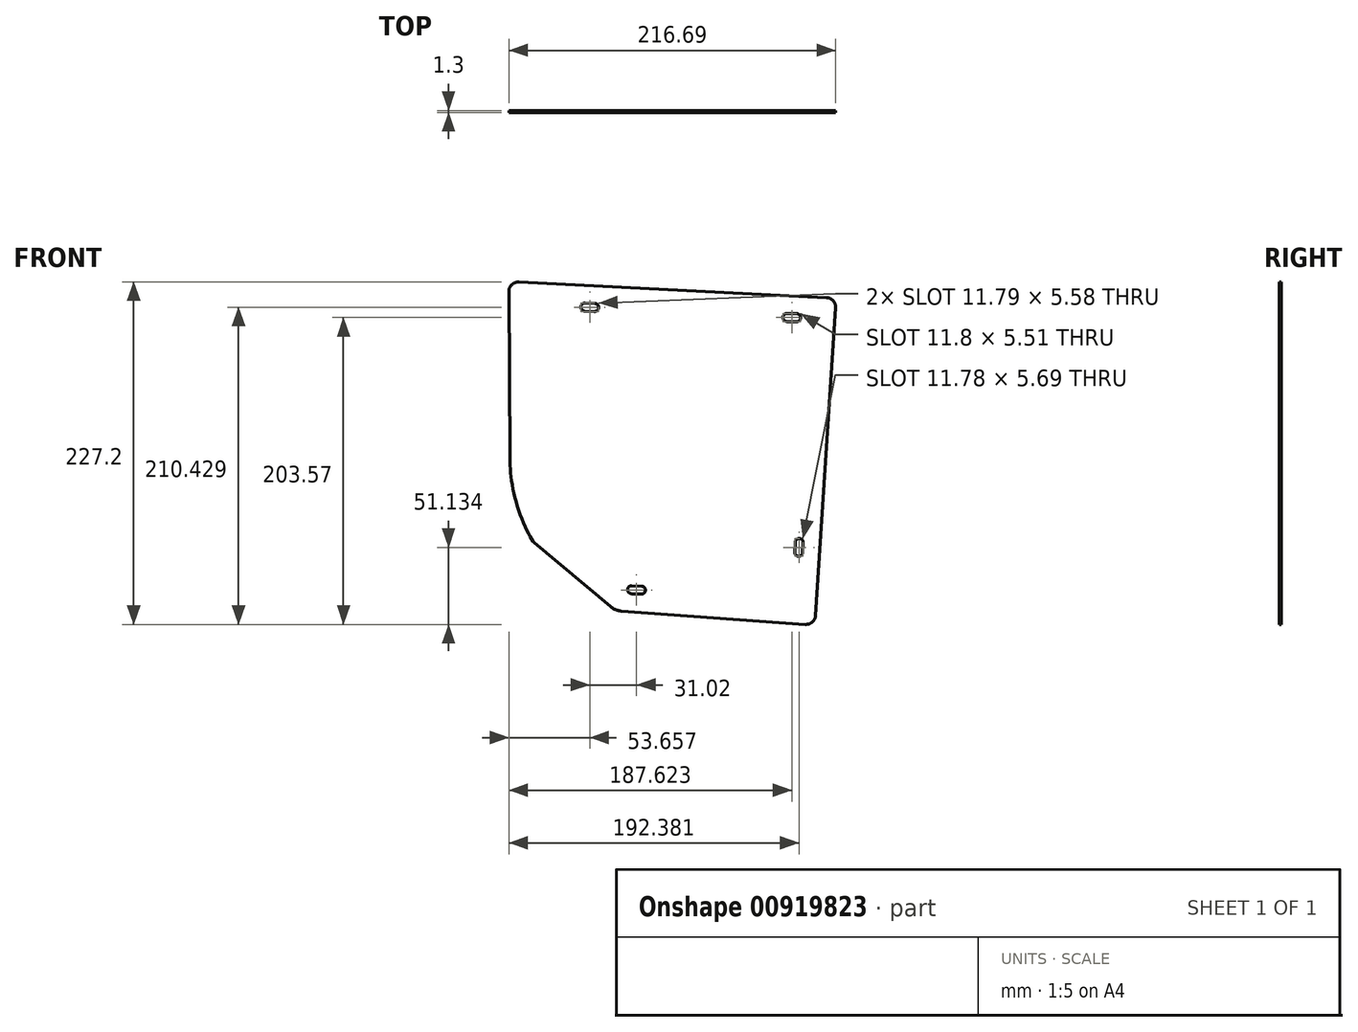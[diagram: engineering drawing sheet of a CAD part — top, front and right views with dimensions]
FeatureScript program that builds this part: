
annotation { "Feature Type Name" : "Feature", "Feature Type Description" : "" }
export const myFeature = defineFeature(function(context is Context, id is Id, definition is map)
    precondition{}
    {
        {
            var Q0;
            Q0=qCreatedBy(makeId("Front.planeOp"),FACE);
            var sketch = newSketch(context, id + "F0", { "sketchPlane" : qUnion([Q0])});
            skLineSegment(sketch, "E0", {"start": v(110.1, -168.08) * mm, "end": v(123.31, 36.08) * mm});
            skLineSegment(sketch, "E1", {"start": v(103.3, -174) * mm, "end": v(-18.7, -165.21) * mm});
            skLineSegment(sketch, "E2", {"start": v(-25.98, -162.25) * mm, "end": v(-76.3, -119.72) * mm});
            skPoint(sketch, "E3", {"position": v(-19.24, -165.17) * mm});
            skArc(sketch, "E4", {"start": v(-86.69, 53.17) * mm, "mid": v(-91.4, 51.42) * mm, "end": v(-93.36, 46.8) * mm});
            skArc(sketch, "E5", {"start": v(103.3, -174) * mm, "mid": v(107.94, -172.45) * mm, "end": v(110.1, -168.08) * mm});
            skArc(sketch, "E6.filletArc", {"start": v(-25.98, -162.25) * mm, "mid": v(-22.57, -164.3) * mm, "end": v(-18.7, -165.21) * mm});
            skArc(sketch, "E7", {"start": v(123.31, 36.08) * mm, "mid": v(121.72, 40.71) * mm, "end": v(117.3, 42.83) * mm});
            skLineSegment(sketch, "E8.trimOffspring", {"start": v(-86.69, 53.17) * mm, "end": v(117.3, 42.83) * mm});
            skFitSpline(sketch, "E9", {"points": [v(-92.68, -63.43) * mm, v(-87.67, -95.63) * mm, v(-76.3, -119.72) * mm], "startDerivative": vector(0.34, -55.65) * mm, "endDerivative": vector(20.09, -16.98) * mm});
            skArc(sketch, "E10", {"start": v(-42.83, 39.2) * mm, "mid": v(-45.6, 36.63) * mm, "end": v(-43.04, 33.87) * mm});
            skArc(sketch, "E11", {"start": v(-36.57, 33.62) * mm, "mid": v(-33.8, 36.18) * mm, "end": v(-36.37, 38.95) * mm});
            skLineSegment(sketch, "E12", {"start": v(-43.04, 33.87) * mm, "end": v(-36.57, 33.62) * mm});
            skLineSegment(sketch, "E13", {"start": v(-42.83, 39.2) * mm, "end": v(-36.37, 38.95) * mm});
            skArc(sketch, "E14", {"start": v(91.1, 32.3) * mm, "mid": v(88.36, 29.71) * mm, "end": v(90.96, 26.97) * mm});
            skArc(sketch, "E15", {"start": v(97.42, 26.8) * mm, "mid": v(100.16, 29.39) * mm, "end": v(97.57, 32.13) * mm});
            skLineSegment(sketch, "E16", {"start": v(90.96, 26.97) * mm, "end": v(97.42, 26.8) * mm});
            skLineSegment(sketch, "E17", {"start": v(91.1, 32.3) * mm, "end": v(97.57, 32.13) * mm});
            skArc(sketch, "E18", {"start": v(-11.81, -148.36) * mm, "mid": v(-14.58, -150.92) * mm, "end": v(-12.02, -153.69) * mm});
            skArc(sketch, "E19", {"start": v(-5.55, -153.94) * mm, "mid": v(-2.79, -151.37) * mm, "end": v(-5.35, -148.6) * mm});
            skLineSegment(sketch, "E20", {"start": v(-12.02, -153.69) * mm, "end": v(-5.55, -153.94) * mm});
            skLineSegment(sketch, "E21", {"start": v(-11.81, -148.36) * mm, "end": v(-5.35, -148.6) * mm});
            skArc(sketch, "E22", {"start": v(96.18, -125.97) * mm, "mid": v(98.7, -128.78) * mm, "end": v(101.5, -126.26) * mm});
            skArc(sketch, "E23", {"start": v(101.86, -119.8) * mm, "mid": v(99.35, -117) * mm, "end": v(96.54, -119.5) * mm});
            skLineSegment(sketch, "E24", {"start": v(101.5, -126.26) * mm, "end": v(101.86, -119.8) * mm});
            skLineSegment(sketch, "E25", {"start": v(96.18, -125.97) * mm, "end": v(96.54, -119.5) * mm});
            skLineSegment(sketch, "E26.trimOffspring", {"start": v(-92.68, -63.43) * mm, "end": v(-93.36, 46.8) * mm});
            skSolve(sketch);
        }
        {
            var Q0;
            Q0=makeQuery(id+"F0.imprint","IMPRINT",FACE,{"disambiguationData":[TD([[makeQuery(id+"F0.imprint","IMPRINT",EDGE,{"derivedFrom":sQuery(id+"F0.wireOp",EDGE,"E0")}),1.0]])]});
            extrude(context, id + "F1", {"entities" : qUnion([Q0]), "depth" : 1.3 * mm, "offsetDistance" : 25.4 * mm});
        }
    });
